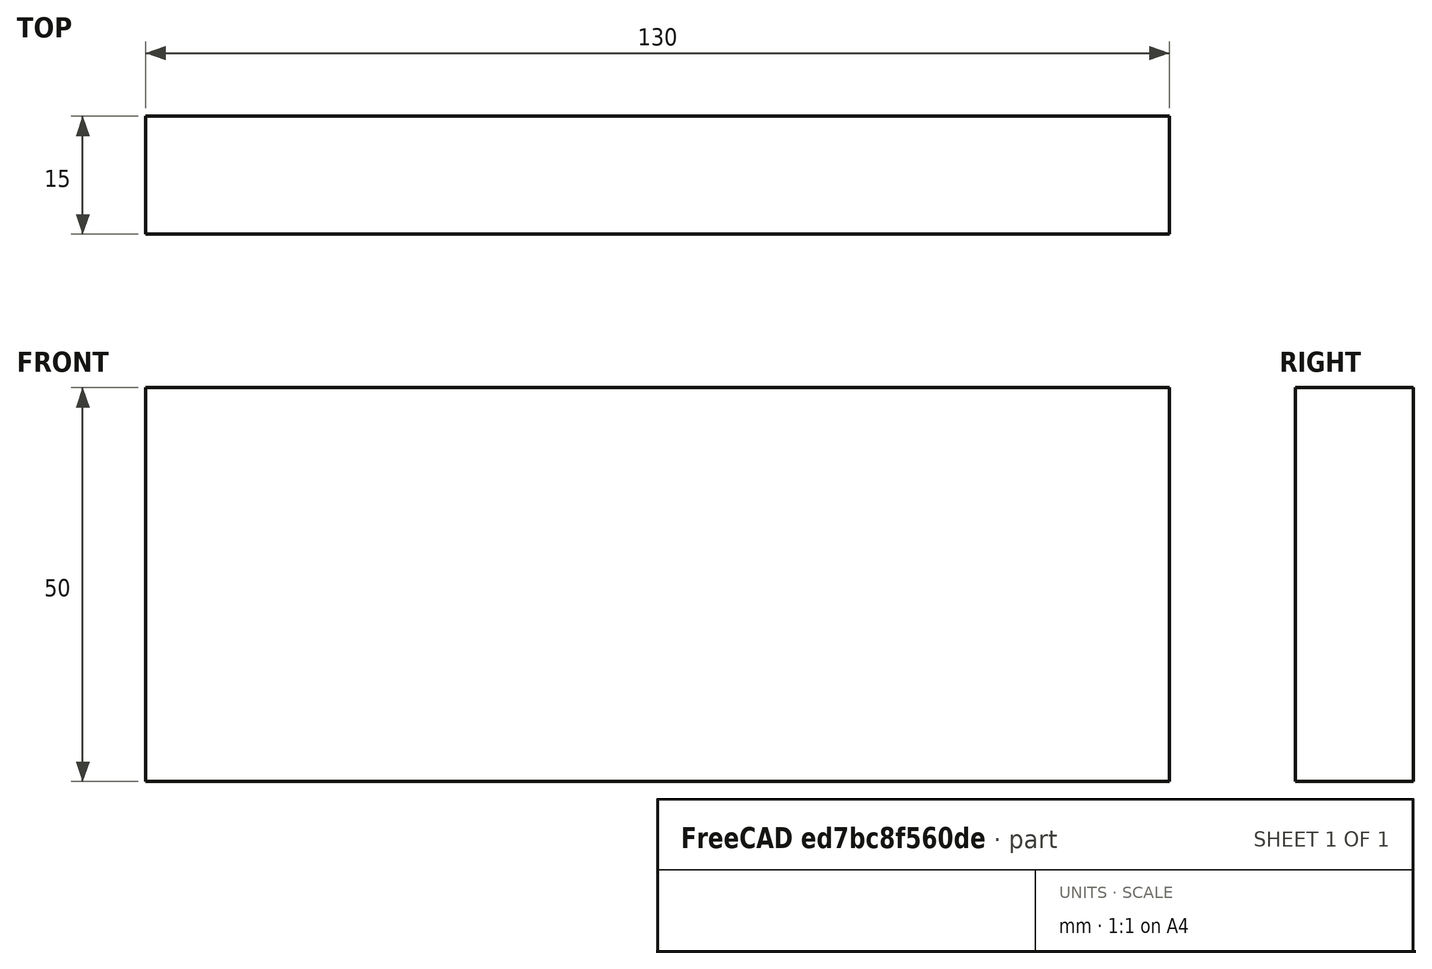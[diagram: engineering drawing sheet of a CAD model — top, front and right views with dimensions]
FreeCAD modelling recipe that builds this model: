
FCSTD DOCUMENT  (FreeCAD 0.15R4671 (Git))
Label: Flat Bar 130x15 EN10058 S235JR
License: All rights reserved
LicenseURL: http://en.wikipedia.org/wiki/All_rights_reserved
objects: Sketcher::SketchObject×1, Part::Extrusion×1
note: 2 computed .brp shape members not serialized (recipe doc carries the construction recipe); baked Part::Feature solids carry a one-line shape summary decoded from their .brp

FEATURE [Sketcher::SketchObject] Sketch
  sketch-geometry (4):
    g0: LineSegment StartX=-65 StartY=-7.5 StartZ=0 EndX=65 EndY=-7.5 EndZ=0
    g1: LineSegment StartX=65 StartY=-7.5 StartZ=0 EndX=65 EndY=7.5 EndZ=0
    g2: LineSegment StartX=65 StartY=7.5 StartZ=0 EndX=-65 EndY=7.5 EndZ=0
    g3: LineSegment StartX=-65 StartY=7.5 StartZ=0 EndX=-65 EndY=-7.5 EndZ=0
  constraints (12):
    c: Coincident(g0,g1)
    c: Coincident(g1,g2)
    c: Coincident(g2,g3)
    c: Coincident(g3,g0)
    c: Horizontal(g0)
    c: Horizontal(g2)
    c: Vertical(g1)
    c: Vertical(g3)
    c: Symmetric(g1,g2,g-2)
    c: Symmetric(g0,g1,g-1)
    c: DistanceY(g1) = 15
    c: DistanceX(g0) = 130
FEATURE [Part::Extrusion] Extrude  label="Flat Bar 130x15 EN10058 S235JR"
  Base = -> Sketch
  Dir = (0,0,50)
  Solid = true
